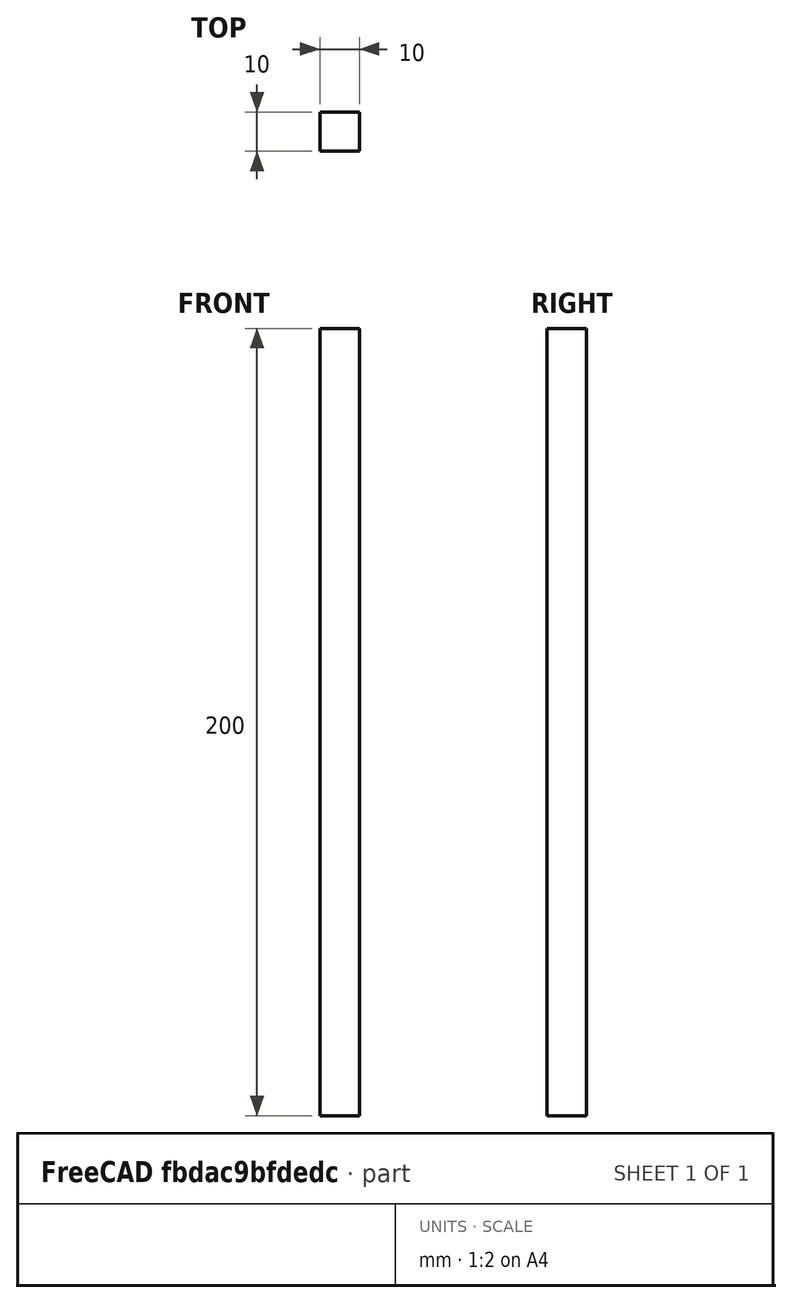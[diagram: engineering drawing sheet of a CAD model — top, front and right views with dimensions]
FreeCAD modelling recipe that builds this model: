
FCSTD DOCUMENT  (FreeCAD 0.20R29410 (Git))
Label: Rod
License: All rights reserved
LicenseURL: http://en.wikipedia.org/wiki/All_rights_reserved
objects: Sketcher::SketchObject×1, PartDesign::Pad×1, PartDesign::Body×1
note: 4 computed .brp shape members not serialized (recipe doc carries the construction recipe); baked Part::Feature solids carry a one-line shape summary decoded from their .brp

FEATURE [Sketcher::SketchObject] Sketch
  FullyConstrained = true
  MapMode = 5
  Support = -> [XY_Plane]
  sketch-geometry (5):
    g0: LineSegment StartX=-5 StartY=5 StartZ=0 EndX=-5 EndY=-5 EndZ=0
    g1: LineSegment StartX=-5 StartY=-5 StartZ=0 EndX=5 EndY=-5 EndZ=0
    g2: LineSegment StartX=5 StartY=-5 StartZ=0 EndX=5 EndY=5 EndZ=0
    g3: LineSegment StartX=5 StartY=5 StartZ=0 EndX=-5 EndY=5 EndZ=0
    g4: GeomPoint X=0 Y=0 Z=0
  constraints (12):
    c: Coincident(g0,g1)
    c: Coincident(g1,g2)
    c: Coincident(g2,g3)
    c: Coincident(g3,g0)
    c: Horizontal(g1)
    c: Horizontal(g3)
    c: Vertical(g0)
    c: Vertical(g2)
    c: Symmetric(g1,g0,g4)
    c: Coincident(g4,g-1)
    c: Equal(g3,g2)
    c: DistanceX(g3,g3) = 10
FEATURE [PartDesign::Pad] Pad
  Direction = (0,0,1)
  Length = 200
  Length2 = 10
  Profile = -> Sketch
  ReferenceAxis = -> Sketch [N_Axis]
  Type = 0
FEATURE [PartDesign::Body] Body
  Group = -> [Sketch,Pad]
  Origin = -> Origin
  Tip = -> Pad
